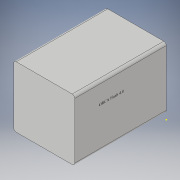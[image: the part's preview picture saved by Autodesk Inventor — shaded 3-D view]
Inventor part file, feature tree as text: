
AUTODESK INVENTOR PART (.ipt)
format: ipt  version: 2019 (Build 230136000, 136)  size: 108,032 bytes
history: native  units: in
note: dims shown in document units (in); Inventor stores cm internally (conversion verified against a paired STEP export)
features: sketch x3, extrude x2, fillet x1
ambient origin geometry x8: Origin, YZ Plane, XZ Plane, XY Plane, X Axis, Y Axis, Z Axis, Center Point
bodies: Solid1 (feature_tree)
feature tree (6):
  extrude  "Extrusion1"  Depth=3.0in
  fillet  "Fillet1"  Radius=4.5in
  sketch  "Sketch2"  dims[d4=0.125in d5=1.5in]
  extrude  "Extrusion2"  Depth=0.125in
  sketch  "Sketch1"  dims[d0=3.0in d1=3.0in d2=4.5in d3=0.0in]
  sketch  "Sketch3"  dims[d6=1.5in d7=0.3in d8=0.0in]
